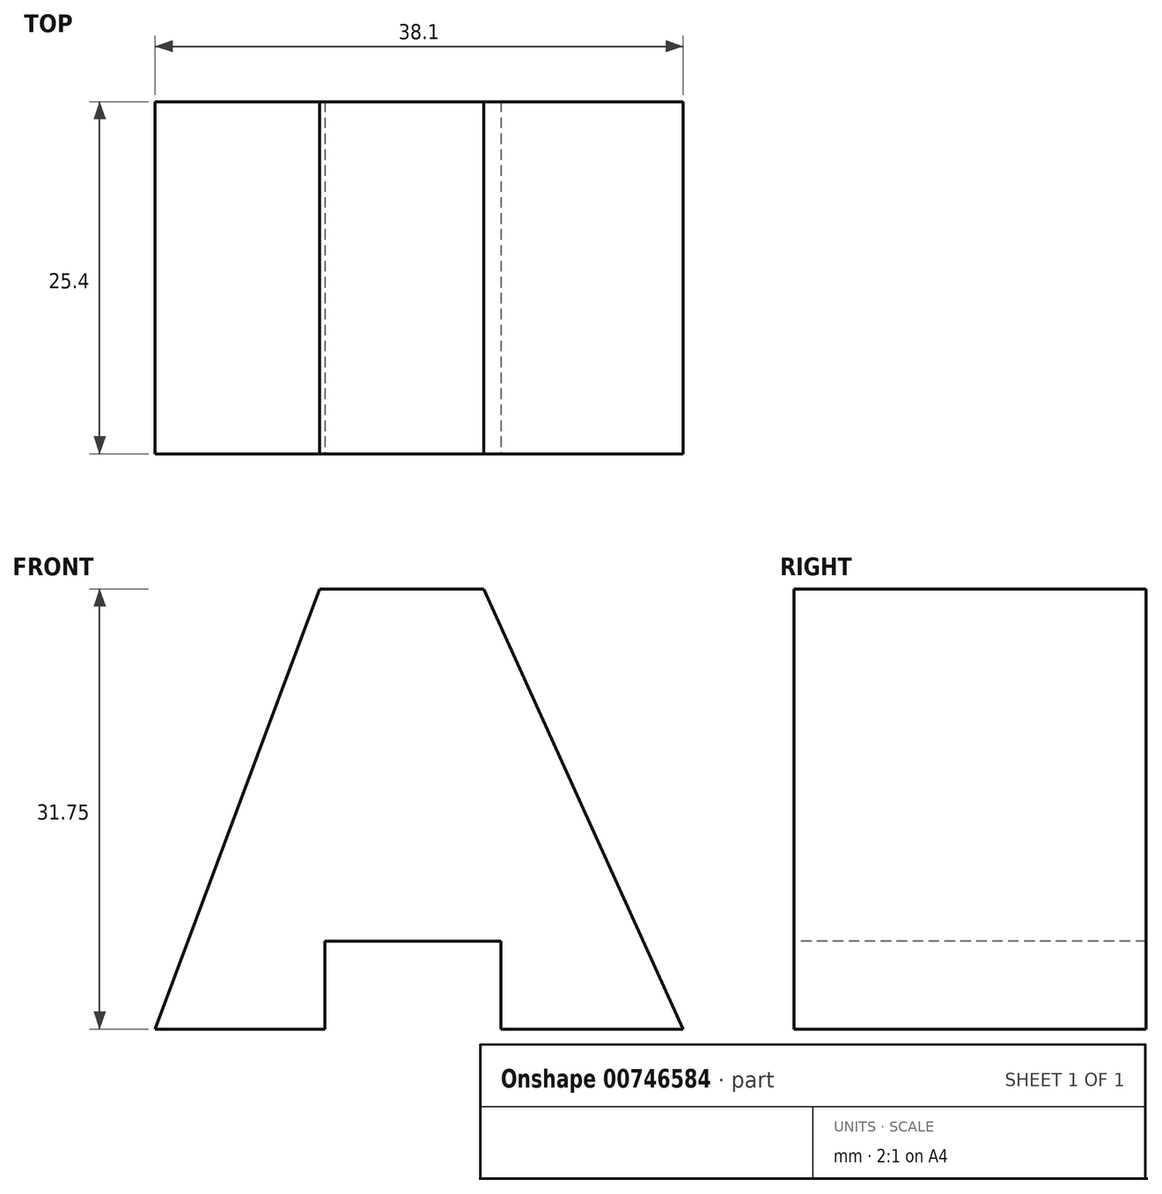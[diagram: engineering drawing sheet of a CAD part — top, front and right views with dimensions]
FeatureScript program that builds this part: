
annotation { "Feature Type Name" : "Feature", "Feature Type Description" : "" }
export const myFeature = defineFeature(function(context is Context, id is Id, definition is map)
    precondition{}
    {
        {
            var Q0;
            Q0=qCreatedBy(makeId("Front.planeOp"),FACE);
            var sketch = newSketch(context, id + "F0", { "sketchPlane" : qUnion([Q0])});
            skLineSegment(sketch, "E0", {"start": v(0, 0) * mm, "end": v(38.1, 0) * mm});
            skLineSegment(sketch, "E1", {"start": v(38.1, 0) * mm, "end": v(38.1, 31.75) * mm});
            skLineSegment(sketch, "E2", {"start": v(38.1, 31.75) * mm, "end": v(0, 31.75) * mm});
            skLineSegment(sketch, "E3", {"start": v(0, 31.75) * mm, "end": v(0, 0) * mm});
            skSolve(sketch);
        }
        {
            var Q0;
            Q0=makeQuery(id+"F0.imprint","IMPRINT",FACE,{"disambiguationData":[TD([[makeQuery(id+"F0.imprint","IMPRINT",EDGE,{"derivedFrom":sQuery(id+"F0.wireOp",EDGE,"E0")}),1.0]])]});
            extrude(context, id + "F1", {"entities" : qUnion([Q0]), "depth" : 25.4 * mm, "offsetDistance" : 25.4 * mm});
        }
        {
            var Q0;
            Q0=makeQuery(id+"F1.opExtrude","CAP_FACE",FACE,{"disambiguationData":[OSD([sQuery(id+"F0.wireOp",EDGE,"E0"),sQuery(id+"F0.wireOp",EDGE,"E1"),sQuery(id+"F0.wireOp",EDGE,"E2"),sQuery(id+"F0.wireOp",EDGE,"E3")])],"isStart":false});
            var sketch = newSketch(context, id + "F2", { "sketchPlane" : qUnion([Q0])});
            skLineSegment(sketch, "E4", {"start": v(23.72, 31.75) * mm, "end": v(38.1, 0) * mm});
            skLineSegment(sketch, "E5", {"start": v(14.11, 31.75) * mm, "end": v(0, 0) * mm});
            skSolve(sketch);
        }
        {
            var Q0;
            {var subQ0=sQuery(id+"F2.wireOp",EDGE,"E4");Q0=makeQuery(id+"F2.imprint","IMPRINT",FACE,{"disambiguationData":[TD([[makeQuery(id+"F2.imprint","IMPRINT",EDGE,{"derivedFrom":subQ0}),1.0]])]});}
            extrude(context, id + "F3", {"entities" : qUnion([Q0]), "operationType" : NewBodyOperationType.REMOVE, "oppositeDirection" : true, "depth" : 25.4 * mm, "offsetDistance" : 25.4 * mm});
        }
        {
            var Q0;
            Q0=makeQuery(id+"F1.opExtrude","CAP_FACE",FACE,{"disambiguationData":[OSD([sQuery(id+"F0.wireOp",EDGE,"E0"),sQuery(id+"F0.wireOp",EDGE,"E1"),sQuery(id+"F0.wireOp",EDGE,"E2"),sQuery(id+"F0.wireOp",EDGE,"E3")])],"isStart":false});
            var sketch = newSketch(context, id + "F4", { "sketchPlane" : qUnion([Q0])});
            skLineSegment(sketch, "E6", {"start": v(11.86, 31.75) * mm, "end": v(0, 0) * mm});
            skSolve(sketch);
        }
        {
            var Q0;
            {var subQ0=sQuery(id+"F4.wireOp",EDGE,"E6");Q0=makeQuery(id+"F4.imprint","IMPRINT",FACE,{"disambiguationData":[TD([[makeQuery(id+"F4.imprint","IMPRINT",EDGE,{"derivedFrom":subQ0}),-1.0]])]});}
            extrude(context, id + "F5", {"entities" : qUnion([Q0]), "operationType" : NewBodyOperationType.REMOVE, "oppositeDirection" : true, "depth" : 25.4 * mm, "offsetDistance" : 25.4 * mm});
        }
        {
            var Q0;
            Q0=makeQuery(id+"F1.opExtrude","CAP_FACE",FACE,{"disambiguationData":[OSD([sQuery(id+"F0.wireOp",EDGE,"E0"),sQuery(id+"F0.wireOp",EDGE,"E1"),sQuery(id+"F0.wireOp",EDGE,"E2"),sQuery(id+"F0.wireOp",EDGE,"E3")])],"isStart":false});
            var sketch = newSketch(context, id + "F6", { "sketchPlane" : qUnion([Q0])});
            skLineSegment(sketch, "E7", {"start": v(12.25, 0) * mm, "end": v(12.25, 6.35) * mm});
            skLineSegment(sketch, "E8", {"start": v(12.25, 6.35) * mm, "end": v(24.95, 6.35) * mm});
            skLineSegment(sketch, "E9", {"start": v(24.95, 6.35) * mm, "end": v(24.95, 0) * mm});
            skLineSegment(sketch, "E10", {"start": v(24.95, 0) * mm, "end": v(12.25, 0) * mm});
            skSolve(sketch);
        }
        {
            var Q0;
            Q0=makeQuery(id+"F6.imprint","IMPRINT",FACE,{"disambiguationData":[TD([[makeQuery(id+"F6.imprint","IMPRINT",EDGE,{"derivedFrom":sQuery(id+"F6.wireOp",EDGE,"E7")}),-1.0]])]});
            extrude(context, id + "F7", {"entities" : qUnion([Q0]), "operationType" : NewBodyOperationType.REMOVE, "oppositeDirection" : true, "depth" : 38.1 * mm, "offsetDistance" : 25.4 * mm});
        }
    });
